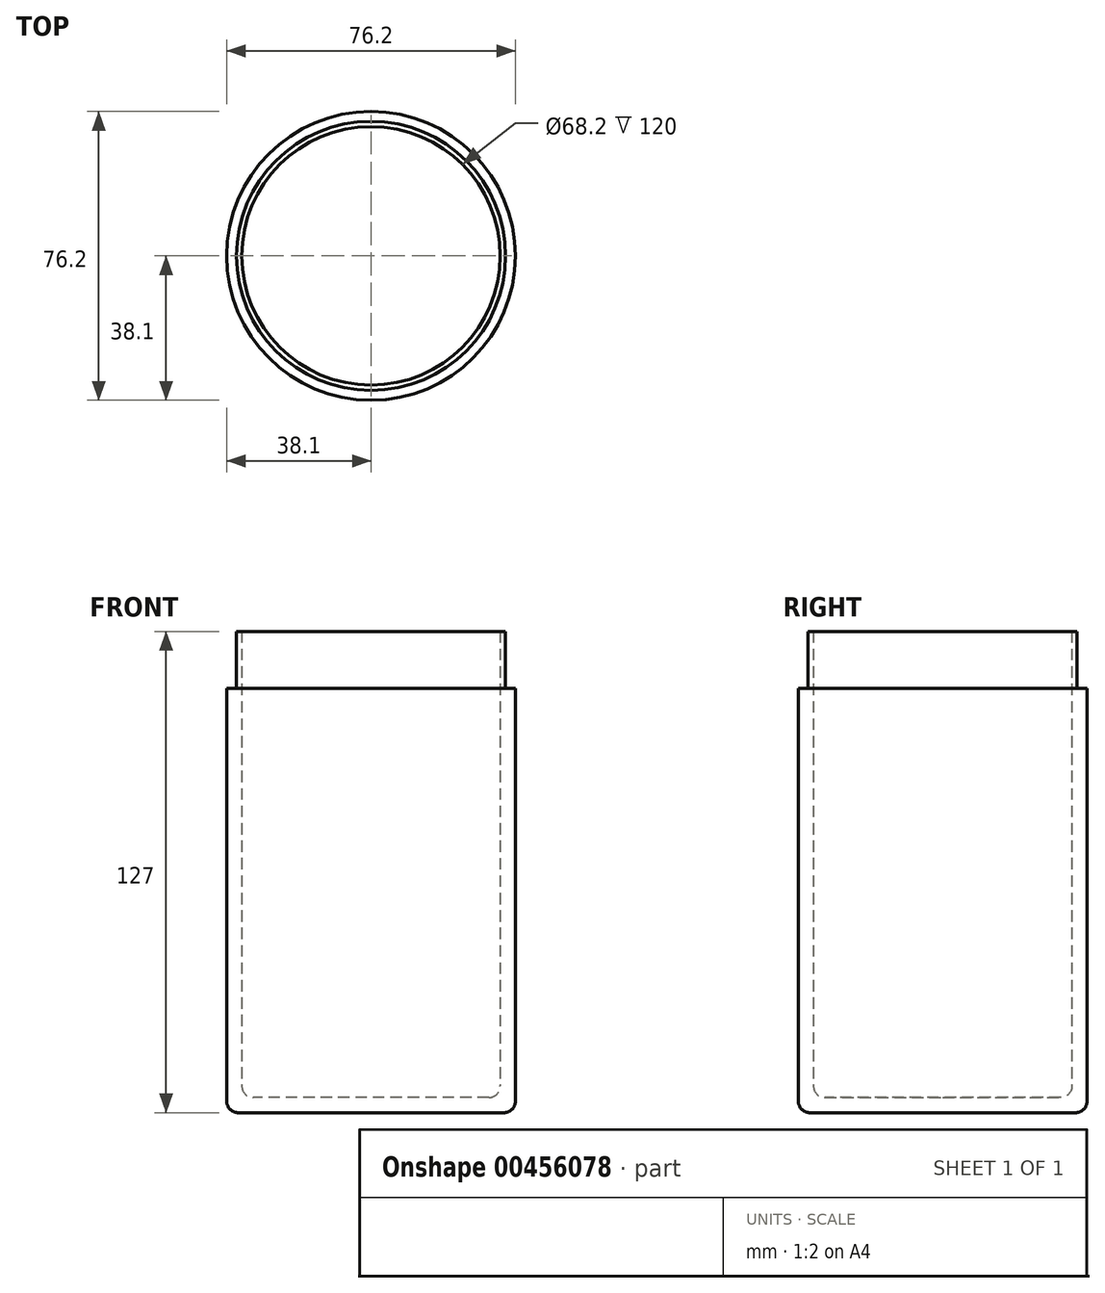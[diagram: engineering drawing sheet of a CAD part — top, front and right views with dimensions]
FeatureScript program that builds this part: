
annotation { "Feature Type Name" : "Feature", "Feature Type Description" : "" }
export const myFeature = defineFeature(function(context is Context, id is Id, definition is map)
    precondition{}
    {
        {
            var Q0;
            Q0=qCreatedBy(makeId("Top.planeOp"),FACE);
            var sketch = newSketch(context, id + "F0", { "sketchPlane" : qUnion([Q0])});
            skCircle(sketch, "E0", {"center": v(0, 0) * mm, "radius": 38.1 * mm});
            skSolve(sketch);
        }
        {
            var Q0;
            Q0=qSketchRegion(id+"F0",true);
            extrude(context, id + "F1", {"entities" : qUnion([Q0]), "depth" : 127 * mm});
        }
        {
            var Q0;
            Q0=makeQuery(id+"F1.opExtrude","CAP_FACE",FACE,{"disambiguationData":[OSD([sQuery(id+"F0.wireOp",EDGE,"E0")])],"isStart":false});
            shell(context, id + "F2", {"entities" : qUnion([Q0]), "thickness" : 4 * mm});
        }
        {
            var Q0;
            Q0=makeQuery(id+"F1.opExtrude","CAP_FACE",FACE,{"disambiguationData":[OSD([sQuery(id+"F0.wireOp",EDGE,"E0")])],"isStart":false});
            var sketch = newSketch(context, id + "F3", { "sketchPlane" : qUnion([Q0])});
            skCircle(sketch, "E1", {"center": v(0, 0) * mm, "radius": 35.5 * mm});
            skSolve(sketch);
        }
        {
            var Q0;
            Q0=makeQuery(id+"F3.imprint","IMPRINT",FACE,{"disambiguationData":[TD([[makeQuery(id+"F3.imprint","IMPRINT",EDGE,{"derivedFrom":sQuery(id+"F3.wireOp",EDGE,"E1")}),-1.0]])]});
            extrude(context, id + "F4", {"entities" : qUnion([Q0]), "operationType" : NewBodyOperationType.REMOVE, "oppositeDirection" : true, "depth" : 15 * mm});
        }
        {
            var Q0;
            Q0=makeQuery(id+"F1.opExtrude","CAP_FACE",FACE,{"disambiguationData":[OSD([sQuery(id+"F0.wireOp",EDGE,"E0")])],"isStart":true});
            var Q1;
            {var subQ0=sQuery(id+"F0.wireOp",EDGE,"E0");Q1=makeQuery(id+"F2.opShell","OFFSET_FACE",FACE,{"disambiguationData":[OSD([subQ0]),TDD([makeQuery(id+"F1.opExtrude","CAP_FACE",FACE,{"disambiguationData":[OSD([subQ0])],"isStart":true})])]});}
            fillet(context, id + "F5", {"entities" : qUnion([Q0, Q1]), "radius" : 3 * mm, "tangentPropagation" : true, "allowEdgeOverflow" : false});
        }
    });
